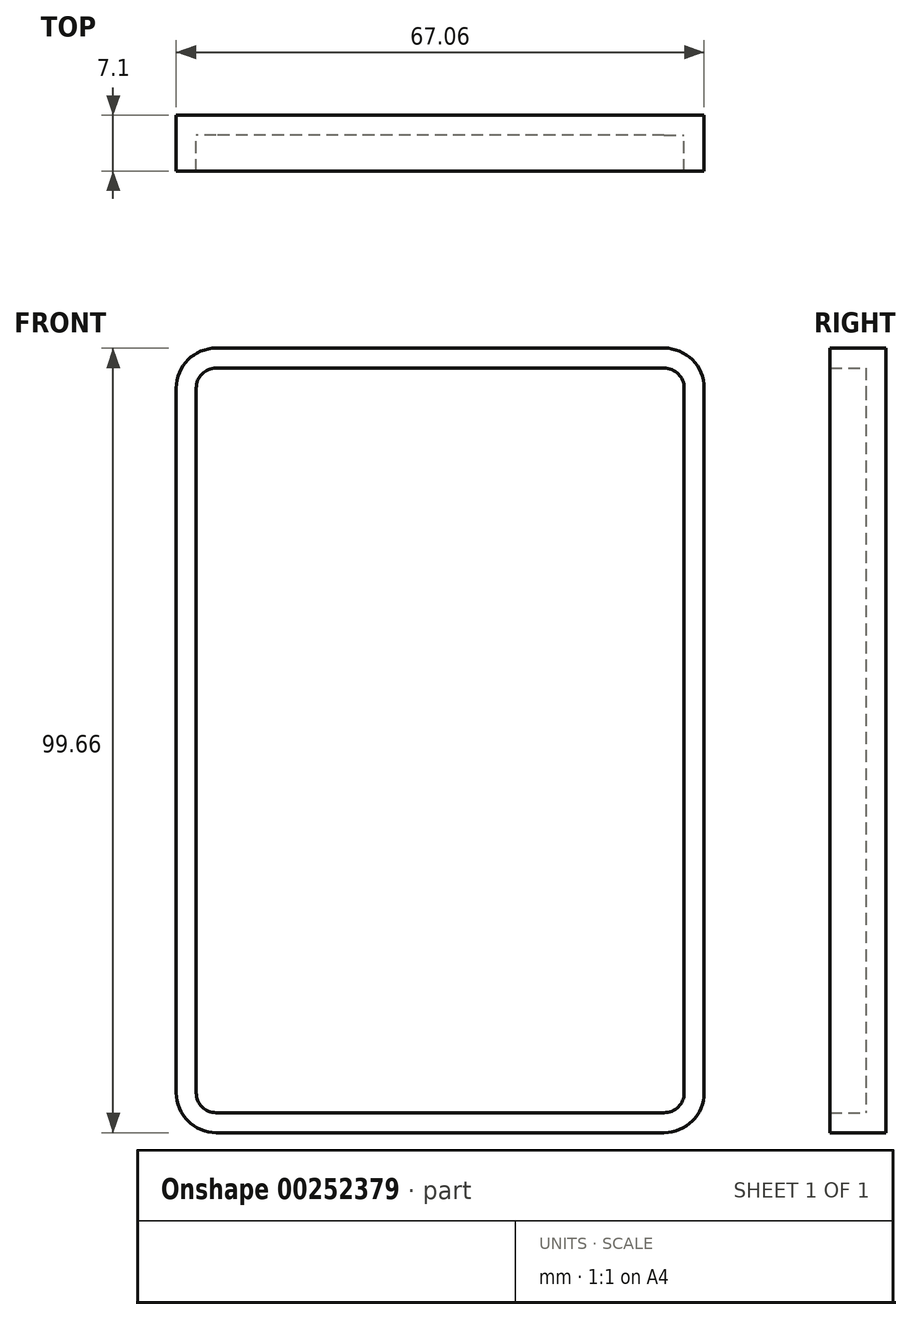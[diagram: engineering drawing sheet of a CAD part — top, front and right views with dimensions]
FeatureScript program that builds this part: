
annotation { "Feature Type Name" : "Feature", "Feature Type Description" : "" }
export const myFeature = defineFeature(function(context is Context, id is Id, definition is map)
    precondition{}
    {
        {
            var Q0;
            Q0=qCreatedBy(makeId("Front.planeOp"),FACE);
            var sketch = newSketch(context, id + "F0", { "sketchPlane" : qUnion([Q0])});
            skLineSegment(sketch, "E0.bottom", {"start": v(33.04, 49.83) * mm, "end": v(-34.02, 49.83) * mm});
            skLineSegment(sketch, "E0.top", {"start": v(33.04, -49.83) * mm, "end": v(-34.02, -49.83) * mm});
            skLineSegment(sketch, "E0.left", {"start": v(33.04, 49.83) * mm, "end": v(33.04, -49.83) * mm});
            skLineSegment(sketch, "E0.right", {"start": v(-34.02, 49.83) * mm, "end": v(-34.02, -49.83) * mm});
            skPoint(sketch, "E0.middle", {"position": v(-0.49, 0) * mm});
            skSolve(sketch);
        }
        {
            var Q0;
            Q0=makeQuery(id+"F0.imprint","IMPRINT",FACE,{"disambiguationData":[TD([[makeQuery(id+"F0.imprint","IMPRINT",EDGE,{"derivedFrom":sQuery(id+"F0.wireOp",EDGE,"E0.bottom")}),1.0]])]});
            extrude(context, id + "F1", {"entities" : qUnion([Q0]), "endBound" : BoundingType.SYMMETRIC, "depth" : 7.1 * mm});
        }
        {
            var Q0;
            Q0=makeQuery(id+"F1.opExtrude","SWEPT_EDGE",EDGE,{"disambiguationData":[OSD([sQuery(id+"F0.wireOp",EDGE,"E0.top"),sQuery(id+"F0.wireOp",EDGE,"E0.right")])]});
            var Q1;
            Q1=makeQuery(id+"F1.opExtrude","SWEPT_EDGE",EDGE,{"disambiguationData":[OSD([sQuery(id+"F0.wireOp",EDGE,"E0.bottom"),sQuery(id+"F0.wireOp",EDGE,"E0.right")])]});
            var Q2;
            Q2=makeQuery(id+"F1.opExtrude","SWEPT_EDGE",EDGE,{"disambiguationData":[OSD([sQuery(id+"F0.wireOp",EDGE,"E0.top"),sQuery(id+"F0.wireOp",EDGE,"E0.left")])]});
            var Q3;
            Q3=makeQuery(id+"F1.opExtrude","SWEPT_EDGE",EDGE,{"disambiguationData":[OSD([sQuery(id+"F0.wireOp",EDGE,"E0.bottom"),sQuery(id+"F0.wireOp",EDGE,"E0.left")])]});
            fillet(context, id + "F2", {"entities" : qUnion([Q0, Q1, Q2, Q3]), "radius" : 5.08 * mm, "tangentPropagation" : true, "allowEdgeOverflow" : false});
        }
        {
            var Q0;
            Q0=makeQuery(id+"F1.opExtrude","CAP_FACE",FACE,{"disambiguationData":[OSD([sQuery(id+"F0.wireOp",EDGE,"E0.bottom"),sQuery(id+"F0.wireOp",EDGE,"E0.top"),sQuery(id+"F0.wireOp",EDGE,"E0.left"),sQuery(id+"F0.wireOp",EDGE,"E0.right")])],"isStart":false});
            shell(context, id + "F3", {"entities" : qUnion([Q0]), "thickness" : 2.54 * mm});
        }
    });
